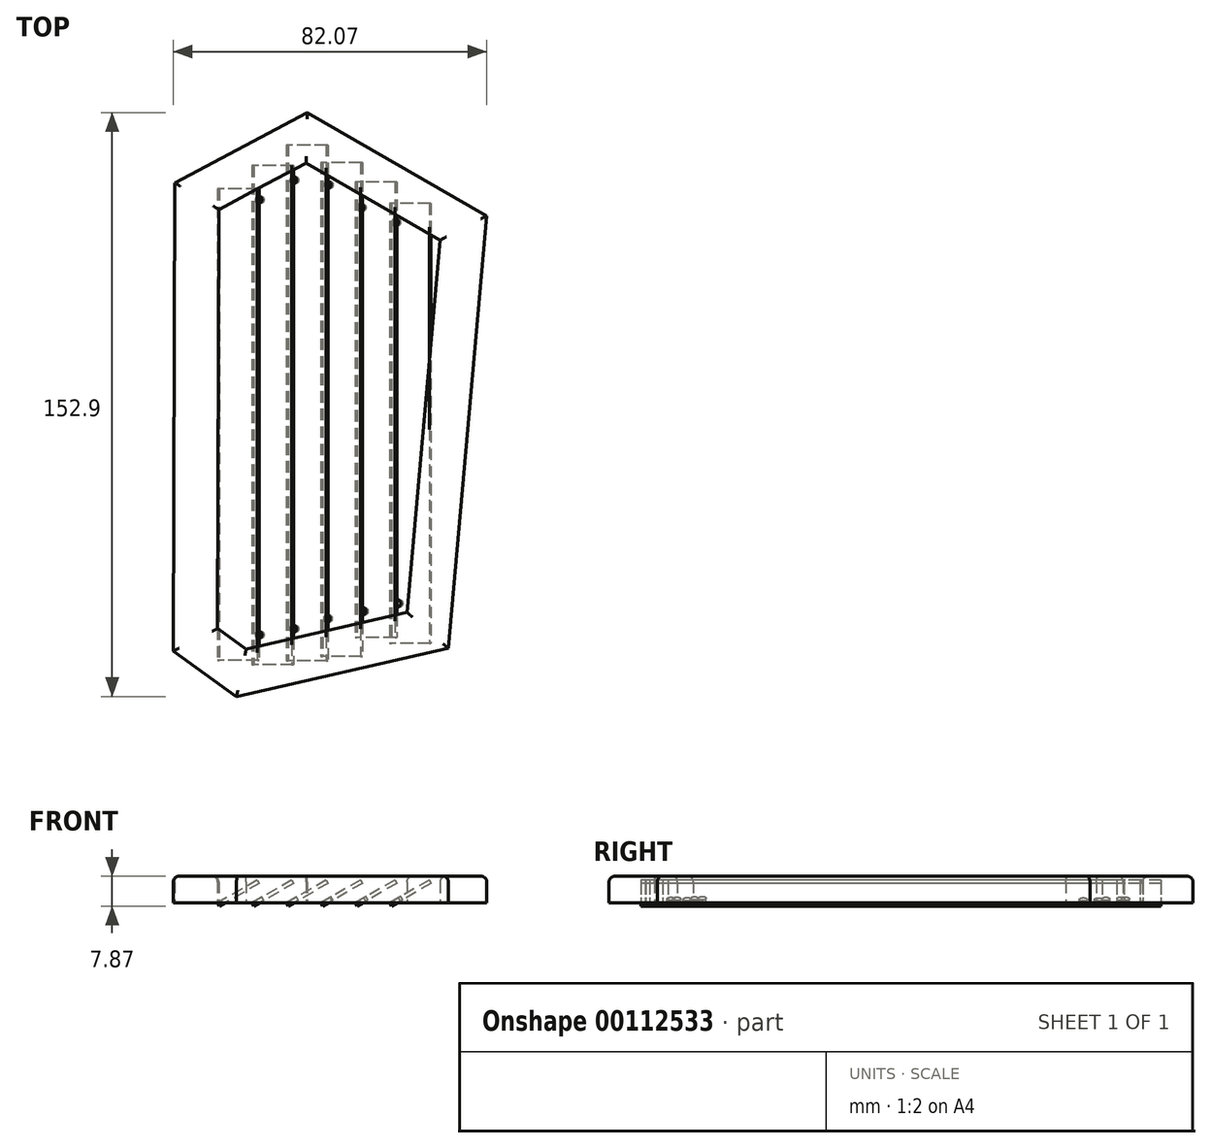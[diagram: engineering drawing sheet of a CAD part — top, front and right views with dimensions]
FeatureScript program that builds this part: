
annotation { "Feature Type Name" : "Feature", "Feature Type Description" : "" }
export const myFeature = defineFeature(function(context is Context, id is Id, definition is map)
    precondition{}
    {
        {
            var Q0;
            Q0=qCreatedBy(makeId("Top.planeOp"),FACE);
            var sketch = newSketch(context, id + "F0", { "sketchPlane" : qUnion([Q0])});
            skLineSegment(sketch, "E0", {"start": v(-11.27, 5.4) * mm, "end": v(-11.6, -117.21) * mm});
            skLineSegment(sketch, "E1", {"start": v(-11.43, -55.9) * mm, "end": v(87.99, -56.18) * mm, "construction": true});
            skLineSegment(sketch, "E2.MirrorCS", {"start": v(0, -111.3) * mm, "end": v(7.48, -116.69) * mm});
            skLineSegment(sketch, "E3.MirrorCS", {"start": v(-11.27, 5.4) * mm, "end": v(23.44, 23.77) * mm});
            skLineSegment(sketch, "E4.MirrorCS", {"start": v(7.48, -116.69) * mm, "end": v(49.62, -107.1) * mm});
            skLineSegment(sketch, "E5.MirrorCS", {"start": v(23.44, 23.77) * mm, "end": v(70.48, -3.23) * mm});
            skLineSegment(sketch, "E6.MirrorCS", {"start": v(-11.6, -117.21) * mm, "end": v(4.95, -129.13) * mm});
            skLineSegment(sketch, "E7.MirrorCS", {"start": v(23.21, 10.56) * mm, "end": v(0.29, -1.58) * mm});
            skLineSegment(sketch, "E8.MirrorCS", {"start": v(58.3, -9.58) * mm, "end": v(23.21, 10.56) * mm});
            skLineSegment(sketch, "E9.MirrorCS", {"start": v(0.29, -1.58) * mm, "end": v(0, -111.3) * mm});
            skLineSegment(sketch, "E10.MirrorCS", {"start": v(60.4, -116.5) * mm, "end": v(4.95, -129.13) * mm});
            skLineSegment(sketch, "E11.MirrorCS", {"start": v(70.48, -3.23) * mm, "end": v(60.4, -116.5) * mm});
            skLineSegment(sketch, "E12.MirrorCS", {"start": v(49.62, -107.1) * mm, "end": v(58.3, -9.58) * mm});
            skLineSegment(sketch, "E13.MirrorCS", {"start": v(-11.6, -117.21) * mm, "end": v(-11.27, 5.4) * mm});
            skSolve(sketch);
        }
        {
            var Q0;
            Q0=qCreatedBy(makeId("Top.planeOp"),FACE);
            var sketch = newSketch(context, id + "F1", { "sketchPlane" : qUnion([Q0])});
            skLineSegment(sketch, "E14.bottom", {"start": v(0, 3.77) * mm, "end": v(1, 3.77) * mm});
            skLineSegment(sketch, "E14.top", {"start": v(0, -119.56) * mm, "end": v(1, -119.56) * mm});
            skLineSegment(sketch, "E14.left", {"start": v(0, 3.77) * mm, "end": v(0, -119.56) * mm});
            skLineSegment(sketch, "E14.right", {"start": v(1, 3.77) * mm, "end": v(1, -119.56) * mm});
            skLineSegment(sketch, "E15.bottom", {"start": v(9, 9.87) * mm, "end": v(10, 9.87) * mm});
            skLineSegment(sketch, "E15.top", {"start": v(9, -120.8) * mm, "end": v(10, -120.8) * mm});
            skLineSegment(sketch, "E15.left", {"start": v(9, 9.87) * mm, "end": v(9, -120.8) * mm});
            skLineSegment(sketch, "E15.right", {"start": v(10, 9.87) * mm, "end": v(10, -120.8) * mm});
            skLineSegment(sketch, "E16.bottom", {"start": v(18, 15.31) * mm, "end": v(19, 15.31) * mm});
            skLineSegment(sketch, "E16.top", {"start": v(18, -119.69) * mm, "end": v(19, -119.69) * mm});
            skLineSegment(sketch, "E16.left", {"start": v(18, 15.31) * mm, "end": v(18, -119.69) * mm});
            skLineSegment(sketch, "E16.right", {"start": v(19, 15.31) * mm, "end": v(19, -119.69) * mm});
            skLineSegment(sketch, "E17.bottom", {"start": v(36, 5.65) * mm, "end": v(37, 5.65) * mm});
            skLineSegment(sketch, "E17.top", {"start": v(36, -113.63) * mm, "end": v(37, -113.63) * mm});
            skLineSegment(sketch, "E17.left", {"start": v(36, 5.65) * mm, "end": v(36, -113.63) * mm});
            skLineSegment(sketch, "E17.right", {"start": v(37, 5.65) * mm, "end": v(37, -113.63) * mm});
            skLineSegment(sketch, "E18.bottom", {"start": v(45, 0) * mm, "end": v(46, 0) * mm});
            skLineSegment(sketch, "E18.top", {"start": v(45, -115.12) * mm, "end": v(46, -115.12) * mm});
            skLineSegment(sketch, "E18.left", {"start": v(45, 0) * mm, "end": v(45, -115.12) * mm});
            skLineSegment(sketch, "E18.right", {"start": v(46, 0) * mm, "end": v(46, -115.12) * mm});
            skLineSegment(sketch, "E19.bottom", {"start": v(27, 10.64) * mm, "end": v(28, 10.64) * mm});
            skLineSegment(sketch, "E19.top", {"start": v(27, -118.57) * mm, "end": v(28, -118.57) * mm});
            skLineSegment(sketch, "E19.left", {"start": v(27, 10.64) * mm, "end": v(27, -118.57) * mm});
            skLineSegment(sketch, "E19.right", {"start": v(28, 10.64) * mm, "end": v(28, -118.57) * mm});
            skLineSegment(sketch, "E20", {"start": v(0, -14.95) * mm, "end": v(50.43, -14.95) * mm, "construction": true});
            skSolve(sketch);
        }
        {
            var Q0;
            Q0=qSketchRegion(id+"F1",true);
            extrude(context, id + "F2", {"entities" : qUnion([Q0]), "depth" : 12 * mm});
        }
        {
            var Q0;
            Q0=makeQuery(id+"F2.opExtrude","SWEPT_BODY",BODY,{"disambiguationData":[OSD([sQuery(id+"F1.wireOp",EDGE,"E14.bottom"),sQuery(id+"F1.wireOp",EDGE,"E14.top"),sQuery(id+"F1.wireOp",EDGE,"E14.left"),sQuery(id+"F1.wireOp",EDGE,"E14.right")])]});
            var Q1;
            Q1=makeQuery(id+"F2.opExtrude","CAP_EDGE",EDGE,{"disambiguationData":[OSD([sQuery(id+"F1.wireOp",EDGE,"E14.left")])],"isStart":true});
            transform(context, id + "F3", {"entities" : qUnion([Q0]), "transformType" : TransformType.ROTATION, "transformAxis" : qUnion([Q1]), "angle" : 60 * degree, "oppositeDirection" : true, "makeCopy" : false});
        }
        {
            var Q0;
            Q0=makeQuery(id+"F2.opExtrude","SWEPT_BODY",BODY,{"disambiguationData":[OSD([sQuery(id+"F1.wireOp",EDGE,"E15.bottom"),sQuery(id+"F1.wireOp",EDGE,"E15.top"),sQuery(id+"F1.wireOp",EDGE,"E15.left"),sQuery(id+"F1.wireOp",EDGE,"E15.right")])]});
            var Q1;
            Q1=makeQuery(id+"F2.opExtrude","CAP_EDGE",EDGE,{"disambiguationData":[OSD([sQuery(id+"F1.wireOp",EDGE,"E15.left")])],"isStart":true});
            transform(context, id + "F4", {"entities" : qUnion([Q0]), "transformType" : TransformType.ROTATION, "transformAxis" : qUnion([Q1]), "angle" : 60 * degree, "oppositeDirection" : true, "makeCopy" : false});
        }
        {
            var Q0;
            Q0=makeQuery(id+"F2.opExtrude","SWEPT_BODY",BODY,{"disambiguationData":[OSD([sQuery(id+"F1.wireOp",EDGE,"E16.bottom"),sQuery(id+"F1.wireOp",EDGE,"E16.top"),sQuery(id+"F1.wireOp",EDGE,"E16.left"),sQuery(id+"F1.wireOp",EDGE,"E16.right")])]});
            var Q1;
            Q1=makeQuery(id+"F2.opExtrude","CAP_EDGE",EDGE,{"disambiguationData":[OSD([sQuery(id+"F1.wireOp",EDGE,"E16.left")])],"isStart":true});
            transform(context, id + "F5", {"entities" : qUnion([Q0]), "transformType" : TransformType.ROTATION, "transformAxis" : qUnion([Q1]), "angle" : 60 * degree, "oppositeDirection" : true, "makeCopy" : false});
        }
        {
            var Q0;
            Q0=makeQuery(id+"F2.opExtrude","SWEPT_BODY",BODY,{"disambiguationData":[OSD([sQuery(id+"F1.wireOp",EDGE,"E19.bottom"),sQuery(id+"F1.wireOp",EDGE,"E19.top"),sQuery(id+"F1.wireOp",EDGE,"E19.left"),sQuery(id+"F1.wireOp",EDGE,"E19.right")])]});
            var Q1;
            Q1=makeQuery(id+"F2.opExtrude","CAP_EDGE",EDGE,{"disambiguationData":[OSD([sQuery(id+"F1.wireOp",EDGE,"E19.left")])],"isStart":true});
            transform(context, id + "F6", {"entities" : qUnion([Q0]), "transformType" : TransformType.ROTATION, "transformAxis" : qUnion([Q1]), "angle" : 60 * degree, "oppositeDirection" : true, "makeCopy" : false});
        }
        {
            var Q0;
            Q0=makeQuery(id+"F2.opExtrude","SWEPT_BODY",BODY,{"disambiguationData":[OSD([sQuery(id+"F1.wireOp",EDGE,"E17.bottom"),sQuery(id+"F1.wireOp",EDGE,"E17.top"),sQuery(id+"F1.wireOp",EDGE,"E17.left"),sQuery(id+"F1.wireOp",EDGE,"E17.right")])]});
            var Q1;
            Q1=makeQuery(id+"F2.opExtrude","CAP_EDGE",EDGE,{"disambiguationData":[OSD([sQuery(id+"F1.wireOp",EDGE,"E17.left")])],"isStart":true});
            transform(context, id + "F7", {"entities" : qUnion([Q0]), "transformType" : TransformType.ROTATION, "transformAxis" : qUnion([Q1]), "angle" : 60 * degree, "oppositeDirection" : true, "makeCopy" : false});
        }
        {
            var Q0;
            Q0=makeQuery(id+"F2.opExtrude","SWEPT_BODY",BODY,{"disambiguationData":[OSD([sQuery(id+"F1.wireOp",EDGE,"E18.bottom"),sQuery(id+"F1.wireOp",EDGE,"E18.top"),sQuery(id+"F1.wireOp",EDGE,"E18.left"),sQuery(id+"F1.wireOp",EDGE,"E18.right")])]});
            var Q1;
            Q1=makeQuery(id+"F2.opExtrude","CAP_EDGE",EDGE,{"disambiguationData":[OSD([sQuery(id+"F1.wireOp",EDGE,"E18.left")])],"isStart":true});
            transform(context, id + "F8", {"entities" : qUnion([Q0]), "transformType" : TransformType.ROTATION, "transformAxis" : qUnion([Q1]), "angle" : 60 * degree, "oppositeDirection" : true, "makeCopy" : false});
        }
        {
            var Q0;
            Q0=makeQuery(id+"F2.opExtrude","SWEPT_FACE",FACE,{"disambiguationData":[OSD([sQuery(id+"F1.wireOp",EDGE,"E15.left")])]});
            var sketch = newSketch(context, id + "F9", { "sketchPlane" : qUnion([Q0])});
            skPoint(sketch, "E21", {"position": v(9.8, -112.96) * mm});
            skPoint(sketch, "E22", {"position": v(9.8, 0.96) * mm});
            skSolve(sketch);
        }
        {
            var Q0;
            Q0=sQuery(id+"F9.wireOp",VERTEX,"E21");
            var Q1;
            Q1=sQuery(id+"F9.wireOp",VERTEX,"E22");
            var Q2;
            Q2=makeQuery(id+"F2.opExtrude","SWEPT_BODY",BODY,{"disambiguationData":[OSD([sQuery(id+"F1.wireOp",EDGE,"E15.bottom"),sQuery(id+"F1.wireOp",EDGE,"E15.top"),sQuery(id+"F1.wireOp",EDGE,"E15.left"),sQuery(id+"F1.wireOp",EDGE,"E15.right")])]});
            hole(context, id + "F10", {"style" : HoleStyle.SIMPLE, "endStyle" : HoleEndStyle.THROUGH, "holeDiameter" : 2 * mm, "locations" : qUnion([Q0, Q1]), "scope" : qUnion([Q2]), "isTappedThrough" : true});
        }
        {
            var Q0;
            Q0=makeQuery(id+"F2.opExtrude","SWEPT_FACE",FACE,{"disambiguationData":[OSD([sQuery(id+"F1.wireOp",EDGE,"E16.left")])]});
            var sketch = newSketch(context, id + "F11", { "sketchPlane" : qUnion([Q0])});
            skPoint(sketch, "E23", {"position": v(17.65, 6.1) * mm});
            skPoint(sketch, "E24", {"position": v(17.65, -111.36) * mm});
            skSolve(sketch);
        }
        {
            var Q0;
            Q0=sQuery(id+"F11.wireOp",VERTEX,"E24");
            var Q1;
            Q1=sQuery(id+"F11.wireOp",VERTEX,"E23");
            var Q2;
            Q2=makeQuery(id+"F2.opExtrude","SWEPT_BODY",BODY,{"disambiguationData":[OSD([sQuery(id+"F1.wireOp",EDGE,"E16.bottom"),sQuery(id+"F1.wireOp",EDGE,"E16.top"),sQuery(id+"F1.wireOp",EDGE,"E16.left"),sQuery(id+"F1.wireOp",EDGE,"E16.right")])]});
            hole(context, id + "F12", {"style" : HoleStyle.SIMPLE, "endStyle" : HoleEndStyle.THROUGH, "holeDiameter" : 2 * mm, "locations" : qUnion([Q0, Q1]), "scope" : qUnion([Q2]), "isTappedThrough" : true});
        }
        {
            var Q0;
            Q0=makeQuery(id+"F2.opExtrude","SWEPT_FACE",FACE,{"disambiguationData":[OSD([sQuery(id+"F1.wireOp",EDGE,"E19.left")])]});
            var sketch = newSketch(context, id + "F13", { "sketchPlane" : qUnion([Q0])});
            skPoint(sketch, "E25", {"position": v(25.5, 4.86) * mm});
            skPoint(sketch, "E26", {"position": v(25.22, -108.7) * mm});
            skSolve(sketch);
        }
        {
            var Q0;
            Q0=sQuery(id+"F13.wireOp",VERTEX,"E25");
            var Q1;
            Q1=sQuery(id+"F13.wireOp",VERTEX,"E26");
            var Q2;
            Q2=makeQuery(id+"F2.opExtrude","SWEPT_BODY",BODY,{"disambiguationData":[OSD([sQuery(id+"F1.wireOp",EDGE,"E19.bottom"),sQuery(id+"F1.wireOp",EDGE,"E19.top"),sQuery(id+"F1.wireOp",EDGE,"E19.left"),sQuery(id+"F1.wireOp",EDGE,"E19.right")])]});
            hole(context, id + "F14", {"style" : HoleStyle.SIMPLE, "endStyle" : HoleEndStyle.THROUGH, "holeDiameter" : 2 * mm, "locations" : qUnion([Q0, Q1]), "scope" : qUnion([Q2]), "isTappedThrough" : true});
        }
        {
            var Q0;
            Q0=makeQuery(id+"F2.opExtrude","SWEPT_FACE",FACE,{"disambiguationData":[OSD([sQuery(id+"F1.wireOp",EDGE,"E17.left")])]});
            var sketch = newSketch(context, id + "F15", { "sketchPlane" : qUnion([Q0])});
            skPoint(sketch, "E27", {"position": v(32.82, -1.08) * mm});
            skPoint(sketch, "E28", {"position": v(33.47, -106.78) * mm});
            skSolve(sketch);
        }
        {
            var Q0;
            Q0=sQuery(id+"F15.wireOp",VERTEX,"E28");
            var Q1;
            Q1=sQuery(id+"F15.wireOp",VERTEX,"E27");
            var Q2;
            Q2=makeQuery(id+"F2.opExtrude","SWEPT_BODY",BODY,{"disambiguationData":[OSD([sQuery(id+"F1.wireOp",EDGE,"E17.bottom"),sQuery(id+"F1.wireOp",EDGE,"E17.top"),sQuery(id+"F1.wireOp",EDGE,"E17.left"),sQuery(id+"F1.wireOp",EDGE,"E17.right")])]});
            hole(context, id + "F16", {"style" : HoleStyle.SIMPLE, "endStyle" : HoleEndStyle.THROUGH, "holeDiameter" : 2 * mm, "locations" : qUnion([Q0, Q1]), "scope" : qUnion([Q2]), "isTappedThrough" : true});
        }
        {
            var Q0;
            Q0=makeQuery(id+"F2.opExtrude","SWEPT_FACE",FACE,{"disambiguationData":[OSD([sQuery(id+"F1.wireOp",EDGE,"E18.left")])]});
            var sketch = newSketch(context, id + "F17", { "sketchPlane" : qUnion([Q0])});
            skPoint(sketch, "E29", {"position": v(41.36, -104.72) * mm});
            skPoint(sketch, "E30", {"position": v(40.68, -4.96) * mm});
            skSolve(sketch);
        }
        {
            var Q0;
            Q0=sQuery(id+"F17.wireOp",VERTEX,"E30");
            var Q1;
            Q1=sQuery(id+"F17.wireOp",VERTEX,"E29");
            var Q2;
            Q2=makeQuery(id+"F2.opExtrude","SWEPT_BODY",BODY,{"disambiguationData":[OSD([sQuery(id+"F1.wireOp",EDGE,"E18.bottom"),sQuery(id+"F1.wireOp",EDGE,"E18.top"),sQuery(id+"F1.wireOp",EDGE,"E18.left"),sQuery(id+"F1.wireOp",EDGE,"E18.right")])]});
            hole(context, id + "F18", {"style" : HoleStyle.SIMPLE, "endStyle" : HoleEndStyle.THROUGH, "holeDiameter" : 2 * mm, "locations" : qUnion([Q0, Q1]), "scope" : qUnion([Q2]), "isTappedThrough" : true});
        }
        {
            var Q0;
            Q0=qSketchRegion(id+"F0",true);
            extrude(context, id + "F19", {"entities" : qUnion([Q0]), "depth" : 7 * mm});
        }
        {
            var Q0;
            Q0=makeQuery(id+"F19.opExtrude","CAP_FACE",FACE,{"disambiguationData":[OSD([sQuery(id+"F0.wireOp",EDGE,"E2.MirrorCS"),sQuery(id+"F0.wireOp",EDGE,"E3.MirrorCS"),sQuery(id+"F0.wireOp",EDGE,"E4.MirrorCS"),sQuery(id+"F0.wireOp",EDGE,"E5.MirrorCS"),sQuery(id+"F0.wireOp",EDGE,"E7.MirrorCS"),sQuery(id+"F0.wireOp",EDGE,"E8.MirrorCS"),sQuery(id+"F0.wireOp",EDGE,"E9.MirrorCS"),sQuery(id+"F0.wireOp",EDGE,"E10.MirrorCS"),sQuery(id+"F0.wireOp",EDGE,"E11.MirrorCS"),sQuery(id+"F0.wireOp",EDGE,"E12.MirrorCS"),sQuery(id+"F0.wireOp",EDGE,"E13.MirrorCS"),sQuery(id+"F0.wireOp",EDGE,"E6.MirrorCS")])],"isStart":false});
            fillet(context, id + "F20", {"entities" : qUnion([Q0]), "radius" : 1.5 * mm, "tangentPropagation" : true, "allowEdgeOverflow" : false});
        }
    });
